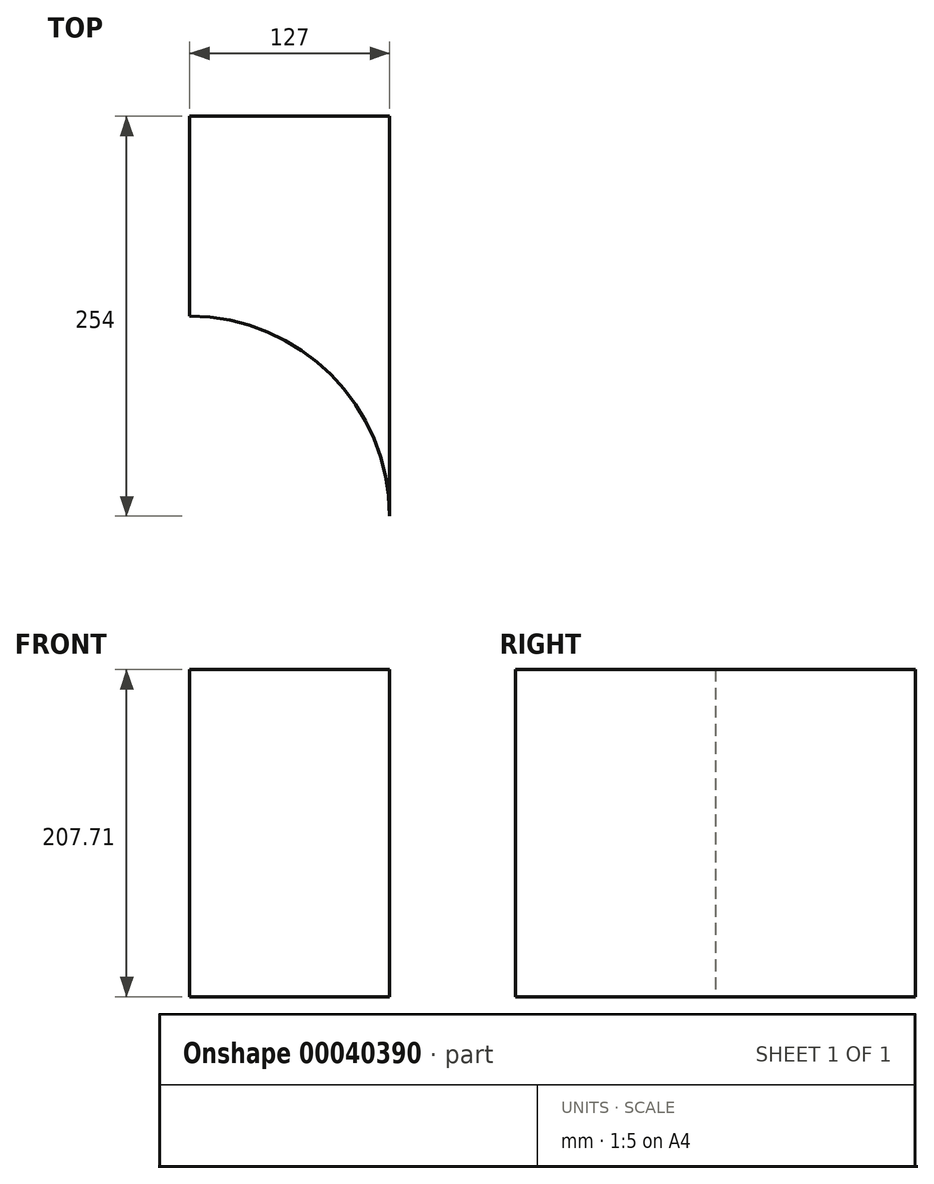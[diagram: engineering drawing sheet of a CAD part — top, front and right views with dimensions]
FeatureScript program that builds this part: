
annotation { "Feature Type Name" : "Feature", "Feature Type Description" : "" }
export const myFeature = defineFeature(function(context is Context, id is Id, definition is map)
    precondition{}
    {
        {
            var Q0;
            Q0=qCreatedBy(makeId("Right.planeOp"),FACE);
            var sketch = newSketch(context, id + "F0", { "sketchPlane" : qUnion([Q0])});
            skLineSegment(sketch, "E0.bottom", {"start": v(0, 0) * mm, "end": v(254, 0) * mm});
            skLineSegment(sketch, "E0.top", {"start": v(0, 207.71) * mm, "end": v(254, 207.71) * mm});
            skLineSegment(sketch, "E0.left", {"start": v(0, 0) * mm, "end": v(0, 207.71) * mm});
            skLineSegment(sketch, "E0.right", {"start": v(254, 0) * mm, "end": v(254, 207.71) * mm});
            skSolve(sketch);
        }
        {
            var Q0;
            Q0 = qSketchRegion(id + "F0", true);
            extrude(context, id + "F1", {"entities" : qUnion([Q0]), "depth" : 127 * mm});
        }
        {
            var Q0;
            Q0=makeQuery(id+"F1.opExtrude","SWEPT_FACE",FACE,{"disambiguationData":[OSD([sQuery(id+"F0.wireOp",EDGE,"E0.bottom")])]});
            var sketch = newSketch(context, id + "F2", { "sketchPlane" : qUnion([Q0])});
            skCircle(sketch, "E1", {"center": v(0, 0) * mm, "radius": 127 * mm});
            skSolve(sketch);
        }
        {
            var Q0;
            Q0 = qSketchRegion(id + "F2", true);
            extrude(context, id + "F3", {"entities" : qUnion([Q0]), "operationType" : NewBodyOperationType.REMOVE, "endBound" : BoundingType.THROUGH_ALL, "oppositeDirection" : true, "depth" : 25.4 * mm});
        }
    });
